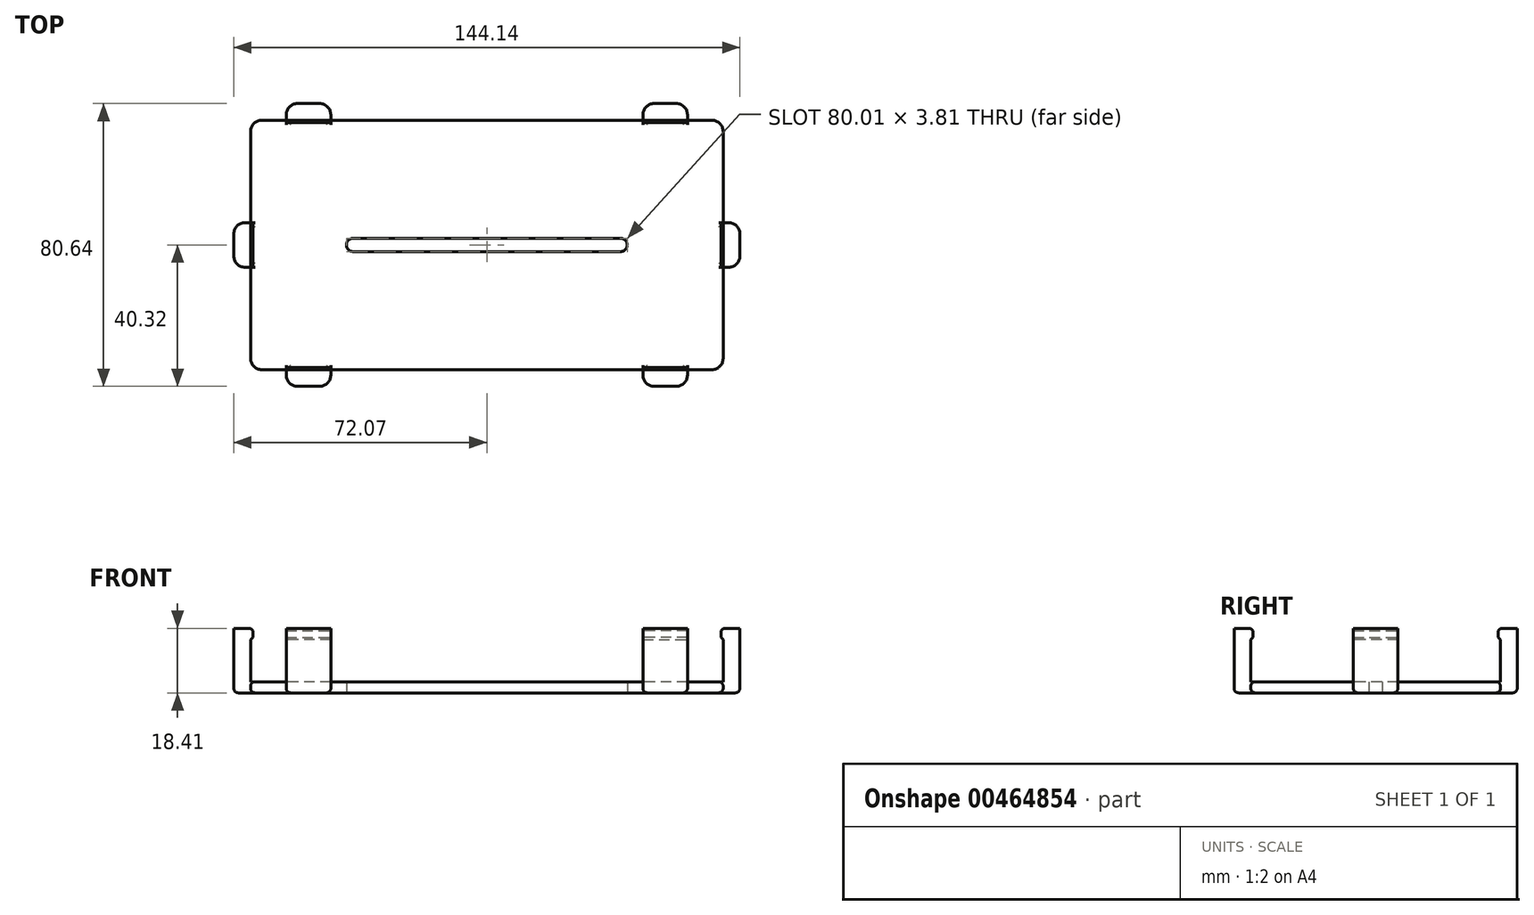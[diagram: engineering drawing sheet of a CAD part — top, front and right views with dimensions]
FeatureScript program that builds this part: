
annotation { "Feature Type Name" : "Feature", "Feature Type Description" : "" }
export const myFeature = defineFeature(function(context is Context, id is Id, definition is map)
    precondition{}
    {
        {
            var Q0;
            Q0=qCreatedBy(makeId("Top.planeOp"),FACE);
            var sketch = newSketch(context, id + "F0", { "sketchPlane" : qUnion([Q0])});
            skLineSegment(sketch, "E0.bottom", {"start": v(64.14, 35.56) * mm, "end": v(-64.14, 35.56) * mm});
            skLineSegment(sketch, "E0.top", {"start": v(64.14, -35.56) * mm, "end": v(-64.14, -35.56) * mm});
            skLineSegment(sketch, "E0.left", {"start": v(67.31, 32.39) * mm, "end": v(67.31, -32.39) * mm});
            skLineSegment(sketch, "E0.right", {"start": v(-67.31, 32.38) * mm, "end": v(-67.31, -32.39) * mm});
            skPoint(sketch, "E0.middle", {"position": v(0, 0) * mm});
            skPoint(sketch, "E1.visualSharp", {"position": v(-67.31, 35.56) * mm});
            skArc(sketch, "E1.filletArc", {"start": v(-64.14, 35.56) * mm, "mid": v(-66.38, 34.63) * mm, "end": v(-67.31, 32.38) * mm});
            skPoint(sketch, "E2.visualSharp", {"position": v(67.31, 35.56) * mm});
            skArc(sketch, "E2.filletArc", {"start": v(67.31, 32.39) * mm, "mid": v(66.38, 34.63) * mm, "end": v(64.14, 35.56) * mm});
            skPoint(sketch, "E3.visualSharp", {"position": v(67.31, -35.56) * mm});
            skArc(sketch, "E3.filletArc", {"start": v(64.14, -35.56) * mm, "mid": v(66.38, -34.63) * mm, "end": v(67.31, -32.39) * mm});
            skPoint(sketch, "E4.visualSharp", {"position": v(-67.31, -35.56) * mm});
            skArc(sketch, "E4.filletArc", {"start": v(-67.31, -32.39) * mm, "mid": v(-66.38, -34.63) * mm, "end": v(-64.14, -35.56) * mm});
            skLineSegment(sketch, "E5", {"start": v(-38.1, 0) * mm, "end": v(38.1, 0) * mm});
            skArc(sketch, "E6.0.startCap", {"start": v(-38.1, -1.9) * mm, "mid": v(-40, 0) * mm, "end": v(-38.1, 1.9) * mm});
            skArc(sketch, "E6.0.endCap", {"start": v(38.1, 1.9) * mm, "mid": v(40, 0) * mm, "end": v(38.1, -1.9) * mm});
            skLineSegment(sketch, "E6.0.left", {"start": v(-38.1, 1.9) * mm, "end": v(38.1, 1.9) * mm});
            skLineSegment(sketch, "E6.0.right", {"start": v(-38.1, -1.9) * mm, "end": v(38.1, -1.9) * mm});
            skSolve(sketch);
        }
        {
            var Q0;
            Q0=makeQuery(id+"F0.imprint","IMPRINT",FACE,{"disambiguationData":[TD([[makeQuery(id+"F0.imprint","IMPRINT",EDGE,{"derivedFrom":sQuery(id+"F0.wireOp",EDGE,"E0.bottom")}),1.0]])]});
            extrude(context, id + "F1", {"entities" : qUnion([Q0]), "depth" : 3.17 * mm});
        }
        {
            var Q0;
            Q0=qCreatedBy(makeId("Top.planeOp"),FACE);
            var sketch = newSketch(context, id + "F2", { "sketchPlane" : qUnion([Q0])});
            skLineSegment(sketch, "E7.bottom", {"start": v(-67.31, 6.35) * mm, "end": v(-68.9, 6.35) * mm});
            skLineSegment(sketch, "E7.top", {"start": v(-67.31, -6.35) * mm, "end": v(-68.9, -6.35) * mm});
            skLineSegment(sketch, "E7.left", {"start": v(-67.31, 6.35) * mm, "end": v(-67.31, -6.35) * mm});
            skLineSegment(sketch, "E7.right", {"start": v(-72.07, 3.17) * mm, "end": v(-72.07, -3.18) * mm});
            skPoint(sketch, "E7.middle", {"position": v(-69.7, 0) * mm});
            skLineSegment(sketch, "E8.bottom", {"start": v(-44.45, -35.56) * mm, "end": v(-57.15, -35.56) * mm});
            skLineSegment(sketch, "E8.top", {"start": v(-47.62, -40.32) * mm, "end": v(-53.97, -40.32) * mm});
            skLineSegment(sketch, "E8.left", {"start": v(-44.45, -35.56) * mm, "end": v(-44.45, -37.15) * mm});
            skLineSegment(sketch, "E8.right", {"start": v(-57.15, -35.56) * mm, "end": v(-57.15, -37.15) * mm});
            skPoint(sketch, "E8.middle", {"position": v(-50.8, -37.94) * mm});
            skLineSegment(sketch, "E9.MirrorCS", {"start": v(-44.45, 35.56) * mm, "end": v(-57.15, 35.56) * mm});
            skLineSegment(sketch, "E10.MirrorCS", {"start": v(-47.62, 40.32) * mm, "end": v(-53.98, 40.32) * mm});
            skLineSegment(sketch, "E11.MirrorCS", {"start": v(-57.15, 35.56) * mm, "end": v(-57.15, 37.15) * mm});
            skLineSegment(sketch, "E12.MirrorCS", {"start": v(-44.45, 35.56) * mm, "end": v(-44.45, 37.15) * mm});
            skLineSegment(sketch, "E13.MirrorCS", {"start": v(44.45, -35.56) * mm, "end": v(44.45, -37.15) * mm});
            skLineSegment(sketch, "E14.MirrorCS", {"start": v(57.15, -35.56) * mm, "end": v(57.15, -37.15) * mm});
            skLineSegment(sketch, "E15.MirrorCS", {"start": v(67.31, -6.35) * mm, "end": v(68.9, -6.35) * mm});
            skLineSegment(sketch, "E16.MirrorCS", {"start": v(67.31, 6.35) * mm, "end": v(68.9, 6.35) * mm});
            skLineSegment(sketch, "E17.MirrorCS", {"start": v(57.15, 35.56) * mm, "end": v(57.15, 37.15) * mm});
            skLineSegment(sketch, "E18.MirrorCS", {"start": v(44.45, 35.56) * mm, "end": v(44.45, 37.15) * mm});
            skLineSegment(sketch, "E19.MirrorCS", {"start": v(47.62, -40.32) * mm, "end": v(53.97, -40.32) * mm});
            skLineSegment(sketch, "E20.MirrorCS", {"start": v(44.45, -35.56) * mm, "end": v(57.15, -35.56) * mm});
            skLineSegment(sketch, "E21.MirrorCS", {"start": v(72.07, 3.17) * mm, "end": v(72.07, -3.18) * mm});
            skLineSegment(sketch, "E22.MirrorCS", {"start": v(67.31, 6.35) * mm, "end": v(67.31, -6.35) * mm});
            skLineSegment(sketch, "E23.MirrorCS", {"start": v(44.45, 35.56) * mm, "end": v(57.15, 35.56) * mm});
            skLineSegment(sketch, "E24.MirrorCS", {"start": v(47.62, 40.32) * mm, "end": v(53.97, 40.32) * mm});
            skPoint(sketch, "E25.MirrorP", {"position": v(50.8, -37.94) * mm});
            skPoint(sketch, "E26.MirrorP", {"position": v(69.7, 0) * mm});
            skPoint(sketch, "E27.middle", {"position": v(-26.96, 18.43) * mm});
            skPoint(sketch, "E28.visualSharp", {"position": v(-57.15, 40.32) * mm});
            skArc(sketch, "E28.filletArc", {"start": v(-53.98, 40.32) * mm, "mid": v(-56.22, 39.4) * mm, "end": v(-57.15, 37.15) * mm});
            skPoint(sketch, "E29.visualSharp", {"position": v(-44.45, 40.32) * mm});
            skArc(sketch, "E29.filletArc", {"start": v(-44.45, 37.15) * mm, "mid": v(-45.38, 39.4) * mm, "end": v(-47.62, 40.32) * mm});
            skPoint(sketch, "E30.visualSharp", {"position": v(-72.07, 6.35) * mm});
            skArc(sketch, "E30.filletArc", {"start": v(-68.9, 6.35) * mm, "mid": v(-71.14, 5.42) * mm, "end": v(-72.07, 3.17) * mm});
            skPoint(sketch, "E31.visualSharp", {"position": v(-72.07, -6.35) * mm});
            skArc(sketch, "E31.filletArc", {"start": v(-72.07, -3.18) * mm, "mid": v(-71.14, -5.42) * mm, "end": v(-68.9, -6.35) * mm});
            skPoint(sketch, "E32.visualSharp", {"position": v(-44.45, -40.32) * mm});
            skArc(sketch, "E32.filletArc", {"start": v(-47.62, -40.32) * mm, "mid": v(-45.38, -39.4) * mm, "end": v(-44.45, -37.15) * mm});
            skPoint(sketch, "E33.visualSharp", {"position": v(-57.15, -40.32) * mm});
            skArc(sketch, "E33.filletArc", {"start": v(-57.15, -37.15) * mm, "mid": v(-56.22, -39.4) * mm, "end": v(-53.97, -40.32) * mm});
            skPoint(sketch, "E34.visualSharp", {"position": v(44.45, -40.32) * mm});
            skArc(sketch, "E34.filletArc", {"start": v(44.45, -37.15) * mm, "mid": v(45.38, -39.4) * mm, "end": v(47.62, -40.32) * mm});
            skPoint(sketch, "E35.visualSharp", {"position": v(57.15, -40.32) * mm});
            skArc(sketch, "E35.filletArc", {"start": v(53.97, -40.32) * mm, "mid": v(56.22, -39.4) * mm, "end": v(57.15, -37.15) * mm});
            skPoint(sketch, "E36.visualSharp", {"position": v(72.07, -6.35) * mm});
            skArc(sketch, "E36.filletArc", {"start": v(68.9, -6.35) * mm, "mid": v(71.14, -5.42) * mm, "end": v(72.07, -3.18) * mm});
            skPoint(sketch, "E37.visualSharp", {"position": v(72.07, 6.35) * mm});
            skArc(sketch, "E37.filletArc", {"start": v(72.07, 3.17) * mm, "mid": v(71.14, 5.42) * mm, "end": v(68.9, 6.35) * mm});
            skPoint(sketch, "E38.visualSharp", {"position": v(57.15, 40.32) * mm});
            skArc(sketch, "E38.filletArc", {"start": v(57.15, 37.15) * mm, "mid": v(56.22, 39.4) * mm, "end": v(53.97, 40.32) * mm});
            skPoint(sketch, "E39.visualSharp", {"position": v(44.45, 40.32) * mm});
            skArc(sketch, "E39.filletArc", {"start": v(47.62, 40.32) * mm, "mid": v(45.38, 39.4) * mm, "end": v(44.45, 37.15) * mm});
            skSolve(sketch);
        }
        {
            var Q0;
            Q0 = qSketchRegion(id + "F2", true);
            extrude(context, id + "F3", {"entities" : qUnion([Q0]), "operationType" : NewBodyOperationType.ADD, "depth" : 15.24 * mm});
        }
        {
            var Q0;
            Q0=makeQuery(id+"F3.opExtrude","CAP_FACE",FACE,{"disambiguationData":[OSD([sQuery(id+"F2.wireOp",EDGE,"E9.MirrorCS"),sQuery(id+"F2.wireOp",EDGE,"E10.MirrorCS"),sQuery(id+"F2.wireOp",EDGE,"E11.MirrorCS"),sQuery(id+"F2.wireOp",EDGE,"E12.MirrorCS"),sQuery(id+"F2.wireOp",EDGE,"E28.filletArc"),sQuery(id+"F2.wireOp",EDGE,"E29.filletArc")])],"isStart":false});
            var sketch = newSketch(context, id + "F4", { "sketchPlane" : qUnion([Q0])});
            skLineSegment(sketch, "E40.bottom", {"start": v(-57.15, 35.56) * mm, "end": v(-44.45, 35.56) * mm});
            skLineSegment(sketch, "E40.top", {"start": v(-53.97, 40.32) * mm, "end": v(-47.62, 40.32) * mm});
            skLineSegment(sketch, "E40.left", {"start": v(-57.15, 35.56) * mm, "end": v(-57.15, 37.15) * mm});
            skLineSegment(sketch, "E40.right", {"start": v(-44.45, 35.56) * mm, "end": v(-44.45, 37.15) * mm});
            skPoint(sketch, "E41.visualSharp", {"position": v(-57.15, 40.32) * mm});
            skArc(sketch, "E41.filletArc", {"start": v(-53.97, 40.32) * mm, "mid": v(-56.22, 39.4) * mm, "end": v(-57.15, 37.15) * mm});
            skPoint(sketch, "E42.visualSharp", {"position": v(-44.45, 40.32) * mm});
            skArc(sketch, "E42.filletArc", {"start": v(-44.45, 37.15) * mm, "mid": v(-45.38, 39.4) * mm, "end": v(-47.62, 40.32) * mm});
            skLineSegment(sketch, "E43.bottom", {"start": v(-67.31, -6.35) * mm, "end": v(-68.9, -6.35) * mm});
            skLineSegment(sketch, "E43.top", {"start": v(-67.31, 6.35) * mm, "end": v(-68.9, 6.35) * mm});
            skLineSegment(sketch, "E43.left", {"start": v(-67.31, -6.35) * mm, "end": v(-67.31, 6.35) * mm});
            skLineSegment(sketch, "E43.right", {"start": v(-72.07, -3.18) * mm, "end": v(-72.07, 3.17) * mm});
            skPoint(sketch, "E44.visualSharp", {"position": v(-72.07, 6.35) * mm});
            skArc(sketch, "E44.filletArc", {"start": v(-68.9, 6.35) * mm, "mid": v(-71.14, 5.42) * mm, "end": v(-72.07, 3.17) * mm});
            skPoint(sketch, "E45.visualSharp", {"position": v(-72.07, -6.35) * mm});
            skArc(sketch, "E45.filletArc", {"start": v(-72.07, -3.18) * mm, "mid": v(-71.14, -5.42) * mm, "end": v(-68.9, -6.35) * mm});
            skLineSegment(sketch, "E46.bottom", {"start": v(-67.31, -6.35) * mm, "end": v(-66.04, -6.35) * mm});
            skLineSegment(sketch, "E46.top", {"start": v(-67.31, 6.35) * mm, "end": v(-66.04, 6.35) * mm});
            skLineSegment(sketch, "E46.right", {"start": v(-66.04, -6.35) * mm, "end": v(-66.04, 6.35) * mm});
            skLineSegment(sketch, "E47.top", {"start": v(-57.15, 34.3) * mm, "end": v(-44.45, 34.3) * mm});
            skLineSegment(sketch, "E47.left", {"start": v(-57.15, 35.56) * mm, "end": v(-57.15, 34.3) * mm});
            skLineSegment(sketch, "E47.right", {"start": v(-44.45, 35.56) * mm, "end": v(-44.45, 34.3) * mm});
            skLineSegment(sketch, "E48.MirrorCS", {"start": v(-57.15, -35.56) * mm, "end": v(-57.15, -34.3) * mm});
            skLineSegment(sketch, "E49.MirrorCS", {"start": v(-44.45, -35.56) * mm, "end": v(-44.45, -34.3) * mm});
            skLineSegment(sketch, "E50.MirrorCS", {"start": v(-44.45, -35.56) * mm, "end": v(-44.45, -37.15) * mm});
            skLineSegment(sketch, "E51.MirrorCS", {"start": v(-57.15, -35.56) * mm, "end": v(-57.15, -37.15) * mm});
            skLineSegment(sketch, "E52.MirrorCS", {"start": v(-57.15, -35.56) * mm, "end": v(-44.45, -35.56) * mm});
            skArc(sketch, "E53.MirrorCS", {"start": v(-44.45, -37.15) * mm, "mid": v(-45.38, -39.4) * mm, "end": v(-47.62, -40.32) * mm});
            skArc(sketch, "E54.MirrorCS", {"start": v(-53.97, -40.32) * mm, "mid": v(-56.22, -39.4) * mm, "end": v(-57.15, -37.15) * mm});
            skLineSegment(sketch, "E55.MirrorCS", {"start": v(-57.15, -34.3) * mm, "end": v(-44.45, -34.3) * mm});
            skPoint(sketch, "E56.MirrorP", {"position": v(-57.15, -40.32) * mm});
            skLineSegment(sketch, "E57.MirrorCS", {"start": v(-53.97, -40.32) * mm, "end": v(-47.62, -40.32) * mm});
            skPoint(sketch, "E58.MirrorP", {"position": v(-44.45, -40.32) * mm});
            skLineSegment(sketch, "E59.MirrorCS", {"start": v(57.15, 35.56) * mm, "end": v(57.15, 34.3) * mm});
            skLineSegment(sketch, "E60.MirrorCS", {"start": v(57.15, 35.56) * mm, "end": v(57.15, 37.15) * mm});
            skLineSegment(sketch, "E61.MirrorCS", {"start": v(67.31, 6.35) * mm, "end": v(66.04, 6.35) * mm});
            skLineSegment(sketch, "E62.MirrorCS", {"start": v(67.31, 6.35) * mm, "end": v(68.9, 6.35) * mm});
            skLineSegment(sketch, "E63.MirrorCS", {"start": v(57.15, -35.56) * mm, "end": v(57.15, -37.15) * mm});
            skLineSegment(sketch, "E64.MirrorCS", {"start": v(57.15, -35.56) * mm, "end": v(57.15, -34.3) * mm});
            skLineSegment(sketch, "E65.MirrorCS", {"start": v(44.45, -35.56) * mm, "end": v(44.45, -34.3) * mm});
            skLineSegment(sketch, "E66.MirrorCS", {"start": v(67.31, -6.35) * mm, "end": v(66.04, -6.35) * mm});
            skLineSegment(sketch, "E67.MirrorCS", {"start": v(44.45, -35.56) * mm, "end": v(44.45, -37.15) * mm});
            skLineSegment(sketch, "E68.MirrorCS", {"start": v(44.45, 35.56) * mm, "end": v(44.45, 37.15) * mm});
            skLineSegment(sketch, "E69.MirrorCS", {"start": v(67.31, -6.35) * mm, "end": v(68.9, -6.35) * mm});
            skLineSegment(sketch, "E70.MirrorCS", {"start": v(44.45, 35.56) * mm, "end": v(44.45, 34.3) * mm});
            skArc(sketch, "E71.MirrorCS", {"start": v(68.9, 6.35) * mm, "mid": v(71.14, 5.42) * mm, "end": v(72.07, 3.17) * mm});
            skArc(sketch, "E72.MirrorCS", {"start": v(53.97, 40.32) * mm, "mid": v(56.22, 39.4) * mm, "end": v(57.15, 37.15) * mm});
            skArc(sketch, "E73.MirrorCS", {"start": v(44.45, 37.15) * mm, "mid": v(45.38, 39.4) * mm, "end": v(47.62, 40.32) * mm});
            skLineSegment(sketch, "E74.MirrorCS", {"start": v(53.97, 40.32) * mm, "end": v(47.62, 40.32) * mm});
            skLineSegment(sketch, "E75.MirrorCS", {"start": v(57.15, 35.56) * mm, "end": v(44.45, 35.56) * mm});
            skArc(sketch, "E76.MirrorCS", {"start": v(53.97, -40.32) * mm, "mid": v(56.22, -39.4) * mm, "end": v(57.15, -37.15) * mm});
            skArc(sketch, "E77.MirrorCS", {"start": v(72.07, -3.18) * mm, "mid": v(71.14, -5.42) * mm, "end": v(68.9, -6.35) * mm});
            skLineSegment(sketch, "E78.MirrorCS", {"start": v(53.97, -40.32) * mm, "end": v(47.62, -40.32) * mm});
            skLineSegment(sketch, "E79.MirrorCS", {"start": v(72.07, -3.18) * mm, "end": v(72.07, 3.17) * mm});
            skArc(sketch, "E80.MirrorCS", {"start": v(44.45, -37.15) * mm, "mid": v(45.38, -39.4) * mm, "end": v(47.62, -40.32) * mm});
            skLineSegment(sketch, "E81.MirrorCS", {"start": v(57.15, -35.56) * mm, "end": v(44.45, -35.56) * mm});
            skLineSegment(sketch, "E82.MirrorCS", {"start": v(67.31, -6.35) * mm, "end": v(67.31, 6.35) * mm});
            skLineSegment(sketch, "E83.MirrorCS", {"start": v(57.15, 34.3) * mm, "end": v(44.45, 34.3) * mm});
            skLineSegment(sketch, "E84.MirrorCS", {"start": v(66.04, -6.35) * mm, "end": v(66.04, 6.35) * mm});
            skPoint(sketch, "E85.MirrorP", {"position": v(72.07, 6.35) * mm});
            skPoint(sketch, "E86.MirrorP", {"position": v(72.07, -6.35) * mm});
            skPoint(sketch, "E87.MirrorP", {"position": v(57.15, -40.32) * mm});
            skPoint(sketch, "E88.MirrorP", {"position": v(57.15, 40.32) * mm});
            skPoint(sketch, "E89.MirrorP", {"position": v(44.45, -40.32) * mm});
            skLineSegment(sketch, "E90.MirrorCS", {"start": v(57.15, -34.3) * mm, "end": v(44.45, -34.3) * mm});
            skPoint(sketch, "E91.MirrorP", {"position": v(44.45, 40.32) * mm});
            skSolve(sketch);
        }
        {
            var Q0;
            Q0=makeQuery(id+"F4.imprint","IMPRINT",FACE,{"disambiguationData":[TD([[makeQuery(id+"F4.imprint","IMPRINT",EDGE,{"derivedFrom":sQuery(id+"F4.wireOp",EDGE,"E43.bottom")}),-1.0]])]});
            var Q1;
            Q1=makeQuery(id+"F4.imprint","IMPRINT",FACE,{"disambiguationData":[TD([[makeQuery(id+"F4.imprint","IMPRINT",EDGE,{"derivedFrom":sQuery(id+"F4.wireOp",EDGE,"E46.bottom")}),1.0]])]});
            var Q2;
            Q2=makeQuery(id+"F4.imprint","IMPRINT",FACE,{"disambiguationData":[TD([[makeQuery(id+"F4.imprint","IMPRINT",EDGE,{"derivedFrom":sQuery(id+"F4.wireOp",EDGE,"E50.MirrorCS")}),-1.0]])]});
            var Q3;
            Q3=makeQuery(id+"F4.imprint","IMPRINT",FACE,{"disambiguationData":[TD([[makeQuery(id+"F4.imprint","IMPRINT",EDGE,{"derivedFrom":sQuery(id+"F4.wireOp",EDGE,"E48.MirrorCS")}),-1.0]])]});
            var Q4;
            Q4=makeQuery(id+"F4.imprint","IMPRINT",FACE,{"disambiguationData":[TD([[makeQuery(id+"F4.imprint","IMPRINT",EDGE,{"derivedFrom":sQuery(id+"F4.wireOp",EDGE,"E40.top")}),1.0]])]});
            var Q5;
            Q5=makeQuery(id+"F4.imprint","IMPRINT",FACE,{"disambiguationData":[TD([[makeQuery(id+"F4.imprint","IMPRINT",EDGE,{"derivedFrom":sQuery(id+"F4.wireOp",EDGE,"E40.bottom")}),1.0]])]});
            var Q6;
            Q6=makeQuery(id+"F4.imprint","IMPRINT",FACE,{"disambiguationData":[TD([[makeQuery(id+"F4.imprint","IMPRINT",EDGE,{"derivedFrom":sQuery(id+"F4.wireOp",EDGE,"E59.MirrorCS")}),-1.0]])]});
            var Q7;
            Q7=makeQuery(id+"F4.imprint","IMPRINT",FACE,{"disambiguationData":[TD([[makeQuery(id+"F4.imprint","IMPRINT",EDGE,{"derivedFrom":sQuery(id+"F4.wireOp",EDGE,"E60.MirrorCS")}),1.0]])]});
            var Q8;
            Q8=makeQuery(id+"F4.imprint","IMPRINT",FACE,{"disambiguationData":[TD([[makeQuery(id+"F4.imprint","IMPRINT",EDGE,{"derivedFrom":sQuery(id+"F4.wireOp",EDGE,"E61.MirrorCS")}),1.0]])]});
            var Q9;
            Q9=makeQuery(id+"F4.imprint","IMPRINT",FACE,{"disambiguationData":[TD([[makeQuery(id+"F4.imprint","IMPRINT",EDGE,{"derivedFrom":sQuery(id+"F4.wireOp",EDGE,"E62.MirrorCS")}),-1.0]])]});
            var Q10;
            Q10=makeQuery(id+"F4.imprint","IMPRINT",FACE,{"disambiguationData":[TD([[makeQuery(id+"F4.imprint","IMPRINT",EDGE,{"derivedFrom":sQuery(id+"F4.wireOp",EDGE,"E63.MirrorCS")}),-1.0]])]});
            var Q11;
            Q11=makeQuery(id+"F4.imprint","IMPRINT",FACE,{"disambiguationData":[TD([[makeQuery(id+"F4.imprint","IMPRINT",EDGE,{"derivedFrom":sQuery(id+"F4.wireOp",EDGE,"E64.MirrorCS")}),1.0]])]});
            extrude(context, id + "F5", {"entities" : qUnion([Q0, Q1, Q2, Q3, Q4, Q5, Q6, Q7, Q8, Q9, Q10, Q11]), "operationType" : NewBodyOperationType.ADD, "depth" : 3.17 * mm});
        }
        {
            var Q0;
            Q0=makeQuery(id+"F5.opExtrude","CAP_EDGE",EDGE,{"disambiguationData":[OSD([sQuery(id+"F4.wireOp",EDGE,"E90.MirrorCS")])],"isStart":true});
            var Q1;
            Q1=makeQuery(id+"F5.opExtrude","CAP_EDGE",EDGE,{"disambiguationData":[OSD([sQuery(id+"F4.wireOp",EDGE,"E90.MirrorCS")])],"isStart":false});
            var Q2;
            Q2=makeQuery(id+"F5.opExtrude","CAP_EDGE",EDGE,{"disambiguationData":[OSD([sQuery(id+"F4.wireOp",EDGE,"E84.MirrorCS")])],"isStart":false});
            var Q3;
            Q3=makeQuery(id+"F5.opExtrude","CAP_EDGE",EDGE,{"disambiguationData":[OSD([sQuery(id+"F4.wireOp",EDGE,"E83.MirrorCS")])],"isStart":false});
            var Q4;
            Q4=makeQuery(id+"F5.opExtrude","CAP_EDGE",EDGE,{"disambiguationData":[OSD([sQuery(id+"F4.wireOp",EDGE,"E55.MirrorCS")])],"isStart":false});
            var Q5;
            Q5=makeQuery(id+"F5.opExtrude","CAP_EDGE",EDGE,{"disambiguationData":[OSD([sQuery(id+"F4.wireOp",EDGE,"E46.right")])],"isStart":false});
            var Q6;
            Q6=makeQuery(id+"F5.opExtrude","CAP_EDGE",EDGE,{"disambiguationData":[OSD([sQuery(id+"F4.wireOp",EDGE,"E47.top")])],"isStart":false});
            var Q7;
            Q7=makeQuery(id+"F5.opExtrude","CAP_EDGE",EDGE,{"disambiguationData":[OSD([sQuery(id+"F4.wireOp",EDGE,"E46.right")])],"isStart":true});
            var Q8;
            Q8=makeQuery(id+"F5.opExtrude","CAP_EDGE",EDGE,{"disambiguationData":[OSD([sQuery(id+"F4.wireOp",EDGE,"E55.MirrorCS")])],"isStart":true});
            var Q9;
            Q9=makeQuery(id+"F5.opExtrude","CAP_EDGE",EDGE,{"disambiguationData":[OSD([sQuery(id+"F4.wireOp",EDGE,"E84.MirrorCS")])],"isStart":true});
            var Q10;
            Q10=makeQuery(id+"F5.opExtrude","CAP_EDGE",EDGE,{"disambiguationData":[OSD([sQuery(id+"F4.wireOp",EDGE,"E83.MirrorCS")])],"isStart":true});
            var Q11;
            Q11=makeQuery(id+"F5.opExtrude","CAP_EDGE",EDGE,{"disambiguationData":[OSD([sQuery(id+"F4.wireOp",EDGE,"E47.top")])],"isStart":true});
            chamfer(context, id + "F6", {"entities" : qUnion([Q0, Q1, Q2, Q3, Q4, Q5, Q6, Q7, Q8, Q9, Q10, Q11]), "width" : 1.27 * mm, "tangentPropagation" : true});
        }
        {
            var Q0;
            Q0=qCreatedBy(makeId("Right.planeOp"),FACE);
            var sketch = newSketch(context, id + "F7", { "sketchPlane" : qUnion([Q0])});
            skLineSegment(sketch, "E92.bottom", {"start": v(-81.14, -79.38) * mm, "end": v(79.36, -79.38) * mm});
            skLineSegment(sketch, "E92.top", {"start": v(-81.14, 77.7) * mm, "end": v(79.36, 77.7) * mm});
            skLineSegment(sketch, "E92.left", {"start": v(-81.14, -79.38) * mm, "end": v(-81.14, 77.7) * mm});
            skLineSegment(sketch, "E92.right", {"start": v(79.36, -79.38) * mm, "end": v(79.36, 77.7) * mm});
            skSolve(sketch);
        }
        {
            var Q0;
            Q0=makeQuery(id+"F5.opExtrude","CAP_FACE",FACE,{"disambiguationData":[OSD([sQuery(id+"F4.wireOp",EDGE,"E40.top"),sQuery(id+"F4.wireOp",EDGE,"E40.left"),sQuery(id+"F4.wireOp",EDGE,"E40.right"),sQuery(id+"F4.wireOp",EDGE,"E41.filletArc"),sQuery(id+"F4.wireOp",EDGE,"E42.filletArc"),sQuery(id+"F4.wireOp",EDGE,"E47.top"),sQuery(id+"F4.wireOp",EDGE,"E47.left"),sQuery(id+"F4.wireOp",EDGE,"E47.right")])],"isStart":false});
            var sketch = newSketch(context, id + "F8", { "sketchPlane" : qUnion([Q0])});
            skLineSegment(sketch, "E93.bottom", {"start": v(-66.68, -34.93) * mm, "end": v(66.68, -34.93) * mm});
            skLineSegment(sketch, "E93.top", {"start": v(-66.68, 34.93) * mm, "end": v(66.68, 34.93) * mm});
            skLineSegment(sketch, "E93.left", {"start": v(-66.68, -34.93) * mm, "end": v(-66.68, 34.93) * mm});
            skLineSegment(sketch, "E93.right", {"start": v(66.68, -34.93) * mm, "end": v(66.68, 34.93) * mm});
            skSolve(sketch);
        }
        {
            var Q0;
            Q0=makeQuery(id+"F8.imprint","IMPRINT",FACE,{"disambiguationData":[TD([[makeQuery(id+"F8.imprint","IMPRINT",EDGE,{"derivedFrom":sQuery(id+"F8.wireOp",EDGE,"E93.bottom")}),1.0]])]});
            extrude(context, id + "F9", {"entities" : qUnion([Q0]), "operationType" : NewBodyOperationType.REMOVE, "oppositeDirection" : true, "depth" : 6.35 * mm});
        }
        {
            var Q0;
            Q0=makeQuery(id+"F3.opExtrude","CAP_EDGE",EDGE,{"disambiguationData":[OSD([sQuery(id+"F2.wireOp",EDGE,"E8.top")])],"isStart":true});
            var Q1;
            Q1=makeQuery(id+"F3.opExtrude","CAP_EDGE",EDGE,{"disambiguationData":[OSD([sQuery(id+"F2.wireOp",EDGE,"E32.filletArc")])],"isStart":true});
            var Q2;
            Q2=makeQuery(id+"F3.opExtrude","CAP_EDGE",EDGE,{"disambiguationData":[OSD([sQuery(id+"F2.wireOp",EDGE,"E33.filletArc")])],"isStart":true});
            var Q3;
            {var subQ0=sQuery(id+"F2.wireOp",EDGE,"E8.left");var subQ2=sQuery(id+"F0.wireOp",EDGE,"E0.top");Q3=makeQuery(id+"F3.boolean.opBoolean","SPLIT",EDGE,{"disambiguationData":[TD([makeQuery(id+"F3.opExtrude","SWEPT_FACE",FACE,{"disambiguationData":[OSD([subQ0])]})])],"derivedFrom":makeQuery(id+"F1.opExtrude","CAP_EDGE",EDGE,{"disambiguationData":[OSD([subQ2])],"isStart":true})});}
            var Q4;
            Q4=makeQuery(id+"F3.opExtrude","CAP_EDGE",EDGE,{"disambiguationData":[OSD([sQuery(id+"F2.wireOp",EDGE,"E34.filletArc")])],"isStart":true});
            var Q5;
            Q5=makeQuery(id+"F3.opExtrude","CAP_EDGE",EDGE,{"disambiguationData":[OSD([sQuery(id+"F2.wireOp",EDGE,"E35.filletArc")])],"isStart":true});
            var Q6;
            {var subQ0=sQuery(id+"F0.wireOp",EDGE,"E3.filletArc");var subQ1=sQuery(id+"F0.wireOp",EDGE,"E0.top");Q6=makeQuery(id+"F3.boolean.opBoolean","SPLIT",EDGE,{"disambiguationData":[TD([makeQuery(id+"F1.opExtrude","SWEPT_FACE",FACE,{"disambiguationData":[OSD([subQ0])]})])],"derivedFrom":makeQuery(id+"F1.opExtrude","CAP_EDGE",EDGE,{"disambiguationData":[OSD([subQ1])],"isStart":true})});}
            var Q7;
            Q7=makeQuery(id+"F3.opExtrude","CAP_EDGE",EDGE,{"disambiguationData":[OSD([sQuery(id+"F2.wireOp",EDGE,"E36.filletArc")])],"isStart":true});
            var Q8;
            {var subQ0=sQuery(id+"F0.wireOp",EDGE,"E2.filletArc");var subQ2=sQuery(id+"F0.wireOp",EDGE,"E0.left");Q8=makeQuery(id+"F3.boolean.opBoolean","SPLIT",EDGE,{"disambiguationData":[TD([makeQuery(id+"F1.opExtrude","SWEPT_FACE",FACE,{"disambiguationData":[OSD([subQ0])]})])],"derivedFrom":makeQuery(id+"F1.opExtrude","CAP_EDGE",EDGE,{"disambiguationData":[OSD([subQ2])],"isStart":true})});}
            var Q9;
            Q9=makeQuery(id+"F3.opExtrude","CAP_EDGE",EDGE,{"disambiguationData":[OSD([sQuery(id+"F2.wireOp",EDGE,"E38.filletArc")])],"isStart":true});
            var Q10;
            {var subQ0=sQuery(id+"F0.wireOp",EDGE,"E0.bottom");var subQ2=sQuery(id+"F2.wireOp",EDGE,"E12.MirrorCS");Q10=makeQuery(id+"F3.boolean.opBoolean","SPLIT",EDGE,{"disambiguationData":[TD([makeQuery(id+"F3.opExtrude","SWEPT_FACE",FACE,{"disambiguationData":[OSD([subQ2])]})])],"derivedFrom":makeQuery(id+"F1.opExtrude","CAP_EDGE",EDGE,{"disambiguationData":[OSD([subQ0])],"isStart":true})});}
            var Q11;
            Q11=makeQuery(id+"F3.opExtrude","CAP_EDGE",EDGE,{"disambiguationData":[OSD([sQuery(id+"F2.wireOp",EDGE,"E10.MirrorCS")])],"isStart":true});
            var Q12;
            {var subQ0=sQuery(id+"F0.wireOp",EDGE,"E1.filletArc");var subQ2=sQuery(id+"F0.wireOp",EDGE,"E0.bottom");Q12=makeQuery(id+"F3.boolean.opBoolean","SPLIT",EDGE,{"disambiguationData":[TD([makeQuery(id+"F1.opExtrude","SWEPT_FACE",FACE,{"disambiguationData":[OSD([subQ0])]})])],"derivedFrom":makeQuery(id+"F1.opExtrude","CAP_EDGE",EDGE,{"disambiguationData":[OSD([subQ2])],"isStart":true})});}
            var Q13;
            Q13=makeQuery(id+"F3.opExtrude","CAP_EDGE",EDGE,{"disambiguationData":[OSD([sQuery(id+"F2.wireOp",EDGE,"E30.filletArc")])],"isStart":true});
            var Q14;
            {var subQ1=sQuery(id+"F0.wireOp",EDGE,"E4.filletArc");var subQ2=sQuery(id+"F0.wireOp",EDGE,"E0.right");Q14=makeQuery(id+"F3.boolean.opBoolean","SPLIT",EDGE,{"disambiguationData":[TD([makeQuery(id+"F1.opExtrude","SWEPT_FACE",FACE,{"disambiguationData":[OSD([subQ1])]})])],"derivedFrom":makeQuery(id+"F1.opExtrude","CAP_EDGE",EDGE,{"disambiguationData":[OSD([subQ2])],"isStart":true})});}
            fillet(context, id + "F10", {"entities" : qUnion([Q0, Q1, Q2, Q3, Q4, Q5, Q6, Q7, Q8, Q9, Q10, Q11, Q12, Q13, Q14]), "radius" : 1.27 * mm, "tangentPropagation" : true, "allowEdgeOverflow" : false});
        }
        {
            var Q0;
            {var subQ0=sQuery(id+"F0.wireOp",EDGE,"E0.left");Q0=makeQuery(id+"F3.boolean.opBoolean","SPLIT",EDGE,{"disambiguationData":[topologyDisambiguationEdgeConnected([makeQuery(id+"F1.opExtrude","CAP_FACE",FACE,{"disambiguationData":[OSD([sQuery(id+"F0.wireOp",EDGE,"E0.bottom"),sQuery(id+"F0.wireOp",EDGE,"E0.top"),subQ0,sQuery(id+"F0.wireOp",EDGE,"E0.right"),sQuery(id+"F0.wireOp",EDGE,"E1.filletArc"),sQuery(id+"F0.wireOp",EDGE,"E2.filletArc"),sQuery(id+"F0.wireOp",EDGE,"E3.filletArc"),sQuery(id+"F0.wireOp",EDGE,"E4.filletArc"),sQuery(id+"F0.wireOp",EDGE,"E6.0.startCap"),sQuery(id+"F0.wireOp",EDGE,"E6.0.endCap"),sQuery(id+"F0.wireOp",EDGE,"E6.0.left"),sQuery(id+"F0.wireOp",EDGE,"E6.0.right")])],"isStart":false}),makeQuery(id+"F3.opExtrude","SWEPT_FACE",FACE,{"disambiguationData":[OSD([sQuery(id+"F2.wireOp",EDGE,"E22.MirrorCS")])]})])],"derivedFrom":makeQuery(id+"F1.opExtrude","CAP_EDGE",EDGE,{"disambiguationData":[OSD([subQ0])],"isStart":false})});}
            var Q1;
            {var subQ0=sQuery(id+"F0.wireOp",EDGE,"E0.top");Q1=makeQuery(id+"F3.boolean.opBoolean","SPLIT",EDGE,{"disambiguationData":[topologyDisambiguationEdgeConnected([makeQuery(id+"F1.opExtrude","CAP_FACE",FACE,{"disambiguationData":[OSD([sQuery(id+"F0.wireOp",EDGE,"E0.bottom"),subQ0,sQuery(id+"F0.wireOp",EDGE,"E0.left"),sQuery(id+"F0.wireOp",EDGE,"E0.right"),sQuery(id+"F0.wireOp",EDGE,"E1.filletArc"),sQuery(id+"F0.wireOp",EDGE,"E2.filletArc"),sQuery(id+"F0.wireOp",EDGE,"E3.filletArc"),sQuery(id+"F0.wireOp",EDGE,"E4.filletArc"),sQuery(id+"F0.wireOp",EDGE,"E6.0.startCap"),sQuery(id+"F0.wireOp",EDGE,"E6.0.endCap"),sQuery(id+"F0.wireOp",EDGE,"E6.0.left"),sQuery(id+"F0.wireOp",EDGE,"E6.0.right")])],"isStart":false}),makeQuery(id+"F3.opExtrude","SWEPT_FACE",FACE,{"disambiguationData":[OSD([sQuery(id+"F2.wireOp",EDGE,"E20.MirrorCS")])]})])],"derivedFrom":makeQuery(id+"F1.opExtrude","CAP_EDGE",EDGE,{"disambiguationData":[OSD([subQ0])],"isStart":false})});}
            var Q2;
            {var subQ0=sQuery(id+"F0.wireOp",EDGE,"E0.top");Q2=makeQuery(id+"F3.boolean.opBoolean","SPLIT",EDGE,{"disambiguationData":[topologyDisambiguationEdgeConnected([makeQuery(id+"F1.opExtrude","CAP_FACE",FACE,{"disambiguationData":[OSD([sQuery(id+"F0.wireOp",EDGE,"E0.bottom"),subQ0,sQuery(id+"F0.wireOp",EDGE,"E0.left"),sQuery(id+"F0.wireOp",EDGE,"E0.right"),sQuery(id+"F0.wireOp",EDGE,"E1.filletArc"),sQuery(id+"F0.wireOp",EDGE,"E2.filletArc"),sQuery(id+"F0.wireOp",EDGE,"E3.filletArc"),sQuery(id+"F0.wireOp",EDGE,"E4.filletArc"),sQuery(id+"F0.wireOp",EDGE,"E6.0.startCap"),sQuery(id+"F0.wireOp",EDGE,"E6.0.endCap"),sQuery(id+"F0.wireOp",EDGE,"E6.0.left"),sQuery(id+"F0.wireOp",EDGE,"E6.0.right")])],"isStart":false}),makeQuery(id+"F3.opExtrude","SWEPT_FACE",FACE,{"disambiguationData":[OSD([sQuery(id+"F2.wireOp",EDGE,"E8.bottom")])]})])],"derivedFrom":makeQuery(id+"F1.opExtrude","CAP_EDGE",EDGE,{"disambiguationData":[OSD([subQ0])],"isStart":false})});}
            var Q3;
            {var subQ0=sQuery(id+"F0.wireOp",EDGE,"E0.right");Q3=makeQuery(id+"F3.boolean.opBoolean","SPLIT",EDGE,{"disambiguationData":[topologyDisambiguationEdgeConnected([makeQuery(id+"F1.opExtrude","CAP_FACE",FACE,{"disambiguationData":[OSD([sQuery(id+"F0.wireOp",EDGE,"E0.bottom"),sQuery(id+"F0.wireOp",EDGE,"E0.top"),sQuery(id+"F0.wireOp",EDGE,"E0.left"),subQ0,sQuery(id+"F0.wireOp",EDGE,"E1.filletArc"),sQuery(id+"F0.wireOp",EDGE,"E2.filletArc"),sQuery(id+"F0.wireOp",EDGE,"E3.filletArc"),sQuery(id+"F0.wireOp",EDGE,"E4.filletArc"),sQuery(id+"F0.wireOp",EDGE,"E6.0.startCap"),sQuery(id+"F0.wireOp",EDGE,"E6.0.endCap"),sQuery(id+"F0.wireOp",EDGE,"E6.0.left"),sQuery(id+"F0.wireOp",EDGE,"E6.0.right")])],"isStart":false}),makeQuery(id+"F3.opExtrude","SWEPT_FACE",FACE,{"disambiguationData":[OSD([sQuery(id+"F2.wireOp",EDGE,"E7.left")])]})])],"derivedFrom":makeQuery(id+"F1.opExtrude","CAP_EDGE",EDGE,{"disambiguationData":[OSD([subQ0])],"isStart":false})});}
            var Q4;
            {var subQ0=sQuery(id+"F0.wireOp",EDGE,"E0.bottom");Q4=makeQuery(id+"F3.boolean.opBoolean","SPLIT",EDGE,{"disambiguationData":[topologyDisambiguationEdgeConnected([makeQuery(id+"F1.opExtrude","CAP_FACE",FACE,{"disambiguationData":[OSD([subQ0,sQuery(id+"F0.wireOp",EDGE,"E0.top"),sQuery(id+"F0.wireOp",EDGE,"E0.left"),sQuery(id+"F0.wireOp",EDGE,"E0.right"),sQuery(id+"F0.wireOp",EDGE,"E1.filletArc"),sQuery(id+"F0.wireOp",EDGE,"E2.filletArc"),sQuery(id+"F0.wireOp",EDGE,"E3.filletArc"),sQuery(id+"F0.wireOp",EDGE,"E4.filletArc"),sQuery(id+"F0.wireOp",EDGE,"E6.0.startCap"),sQuery(id+"F0.wireOp",EDGE,"E6.0.endCap"),sQuery(id+"F0.wireOp",EDGE,"E6.0.left"),sQuery(id+"F0.wireOp",EDGE,"E6.0.right")])],"isStart":false}),makeQuery(id+"F3.opExtrude","SWEPT_FACE",FACE,{"disambiguationData":[OSD([sQuery(id+"F2.wireOp",EDGE,"E9.MirrorCS")])]})])],"derivedFrom":makeQuery(id+"F1.opExtrude","CAP_EDGE",EDGE,{"disambiguationData":[OSD([subQ0])],"isStart":false})});}
            var Q5;
            {var subQ0=sQuery(id+"F0.wireOp",EDGE,"E0.bottom");Q5=makeQuery(id+"F3.boolean.opBoolean","SPLIT",EDGE,{"disambiguationData":[topologyDisambiguationEdgeConnected([makeQuery(id+"F1.opExtrude","CAP_FACE",FACE,{"disambiguationData":[OSD([subQ0,sQuery(id+"F0.wireOp",EDGE,"E0.top"),sQuery(id+"F0.wireOp",EDGE,"E0.left"),sQuery(id+"F0.wireOp",EDGE,"E0.right"),sQuery(id+"F0.wireOp",EDGE,"E1.filletArc"),sQuery(id+"F0.wireOp",EDGE,"E2.filletArc"),sQuery(id+"F0.wireOp",EDGE,"E3.filletArc"),sQuery(id+"F0.wireOp",EDGE,"E4.filletArc"),sQuery(id+"F0.wireOp",EDGE,"E6.0.startCap"),sQuery(id+"F0.wireOp",EDGE,"E6.0.endCap"),sQuery(id+"F0.wireOp",EDGE,"E6.0.left"),sQuery(id+"F0.wireOp",EDGE,"E6.0.right")])],"isStart":false}),makeQuery(id+"F3.opExtrude","SWEPT_FACE",FACE,{"disambiguationData":[OSD([sQuery(id+"F2.wireOp",EDGE,"E23.MirrorCS")])]})])],"derivedFrom":makeQuery(id+"F1.opExtrude","CAP_EDGE",EDGE,{"disambiguationData":[OSD([subQ0])],"isStart":false})});}
            fillet(context, id + "F11", {"entities" : qUnion([Q0, Q1, Q2, Q3, Q4, Q5]), "radius" : 1.27 * mm, "tangentPropagation" : true, "allowEdgeOverflow" : false});
        }
    });
